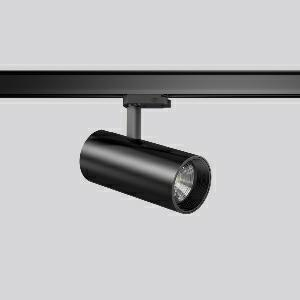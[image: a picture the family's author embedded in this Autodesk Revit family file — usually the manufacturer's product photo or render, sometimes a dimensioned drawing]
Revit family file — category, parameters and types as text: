
# Revit family: deecos_s_mini_742201_003_3_357d
name_source: partatom
category: Lighting Fixtures
units: mm (PartAtom-declared; Revit-internal decimal feet)

## family parameters
Cut with Voids When Loaded = No
Host = Face
Light Source = No
Part Type = Normal
Room Calculation Point = No
Round Connector Dimension = Use Diameter
Shared = No

## types (1)
- DEECOS S mini (1 x LED Modul 935, 2300 lm, 3500)
    Apparent Load = 20 VA
    Approval mark = CE
    CIE Flux Codes = 80 99 100 100 100
    Color Rendering = 92
    Color Temperature = 3500
    Default Elevation = 1800 mm
    Description = Series: DEECOS S mini
LED surface-mounted projector in modern design with no visible cooling ribs. Housing: die-cast aluminium, powder-coated. Rotation range: 356°. Swivel range: 90°. Black plastic ring and recessed LED to prevent glare from the side. Optical assembly with lens made of plastic (polycarbonate) for the best homogeneous light distribution - can be changed without tools. Best colour rendering index Ra>90. With multi adaptor for 3-circuit tracks 230 V. Suitable for Track on ceiling, Wall track. High quality converter without flickering and stroboscopic effect. The following accessories can be mounted without use of tools: interchangeable lenses, decorative glasses, honeycomb louvre, clear and frosted diffusers, white interchangeable plastic ring. 
Colour: deep black, matt (RAL 9005)
Diameter: 87 mm
Height: 214 mm
Lamp: LED
Socket: without socket
Colour temperature: 3500K
Colour rendering index (CRI): 92
System power: 20 W
Rated luminous flux: 2300 lm
Luminous efficiency: 115 lm/W
Control gear: Regulated power supply
Protection class: I
Type of protection: IP 20
    Height = 214 mm
    Lamp = 1 x LED Modul 935
    Lamp Light Flux = 2300 lm
    Lamp count = 1
    Length = 87 mm
    Lifetime = 50000 h
    Luminous efficacy = 115 lm/W
    Manufacturer = RZB
    ModVariant = No
    Model = 742201.003.3
    Mounting Place = Ceiling
    Mounting Type = Rail mounted
    Number of Poles = 1
    OnlyDefault = Yes
    Power Factor = 1
    Product Name = DEECOS S mini
    Product group = Track mounted projectors
    ProductGroupID = 301
    Protection Class = Protection class I
    Protection Degree = IP 20
    RLX_Detail_Level = 1
    RLX_Emergency_Light_Flux = 0 lm
    RLX_Emergency_Type = 0
    RLX_Emergency_Type_DB = No
    RlxData = <blob elided: 38693 chars, md5=98fdc730>
    Socket = socket
    Standby Power = 0 W
    System Light Flux = 2300 lm
    System Power = 20 W
    Type Comments = Product without accessories
    Type Image = 741930.003.jpg
    URL = http://relux.com
    VarID = ---
    Voltage = 230 V
    Voltage Range = 220-240 V
    Weight = 0.00 kg
    Width = 0 mm  [stored 0 ft]

note: [stored X ft] marks values corroborated as IEEE doubles in the binary element streams (Revit-internal decimal feet)

## geometry (parser evidence)
native form markers: Blend x4, Sweep x13
no freeform markers — native parametric forms only
